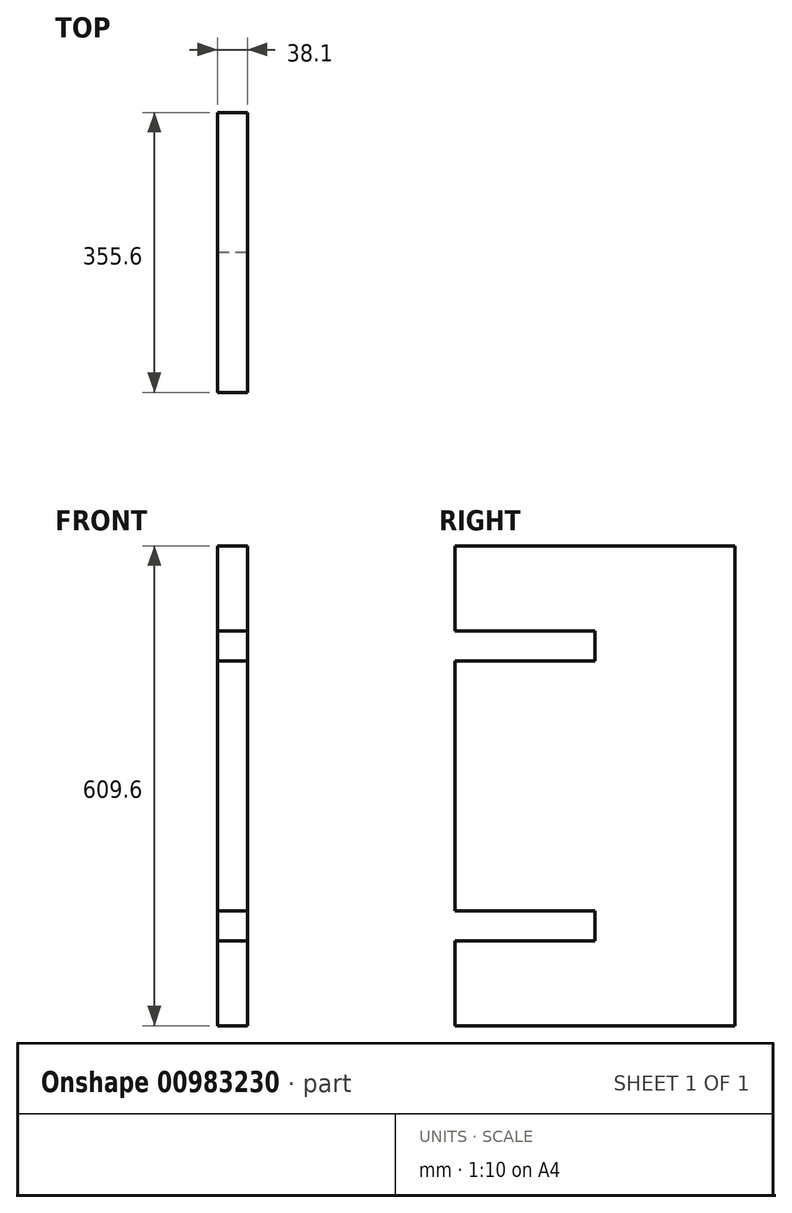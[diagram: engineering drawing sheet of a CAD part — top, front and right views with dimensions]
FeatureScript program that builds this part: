
annotation { "Feature Type Name" : "Feature", "Feature Type Description" : "" }
export const myFeature = defineFeature(function(context is Context, id is Id, definition is map)
    precondition{}
    {
        {
            var Q0;
            Q0=qCreatedBy(makeId("Right.planeOp"),FACE);
            var sketch = newSketch(context, id + "F0", { "sketchPlane" : qUnion([Q0])});
            skLineSegment(sketch, "E0.bottom", {"start": v(177.8, -304.8) * mm, "end": v(-177.8, -304.8) * mm});
            skLineSegment(sketch, "E0.top", {"start": v(177.8, 304.8) * mm, "end": v(-177.8, 304.8) * mm});
            skLineSegment(sketch, "E0.left", {"start": v(177.8, -304.8) * mm, "end": v(177.8, 304.8) * mm});
            skLineSegment(sketch, "E0.right", {"start": v(-177.8, -304.8) * mm, "end": v(-177.8, 304.8) * mm});
            skPoint(sketch, "E0.middle", {"position": v(0, 0) * mm});
            skLineSegment(sketch, "E1.bottom", {"start": v(-177.8, 196.85) * mm, "end": v(0, 196.85) * mm});
            skLineSegment(sketch, "E1.top", {"start": v(-177.8, 158.75) * mm, "end": v(0, 158.75) * mm});
            skLineSegment(sketch, "E1.left", {"start": v(-177.8, 196.85) * mm, "end": v(-177.8, 158.75) * mm});
            skLineSegment(sketch, "E1.right", {"start": v(0, 196.85) * mm, "end": v(0, 158.75) * mm});
            skLineSegment(sketch, "E2.MirrorCS", {"start": v(0, -196.85) * mm, "end": v(0, -158.75) * mm});
            skLineSegment(sketch, "E3.MirrorCS", {"start": v(-177.8, -196.85) * mm, "end": v(-177.8, -158.75) * mm});
            skLineSegment(sketch, "E4.MirrorCS", {"start": v(-177.8, -196.85) * mm, "end": v(0, -196.85) * mm});
            skLineSegment(sketch, "E5.MirrorCS", {"start": v(-177.8, -158.75) * mm, "end": v(0, -158.75) * mm});
            skSolve(sketch);
        }
        {
            var Q0;
            {var subQ7=sQuery(id+"F0.wireOp",EDGE,"E0.bottom");Q0=makeQuery(id+"F0.imprint","IMPRINT",FACE,{"disambiguationData":[TD([[makeQuery(id+"F0.imprint","IMPRINT",EDGE,{"derivedFrom":subQ7}),-1.0]])]});}
            extrude(context, id + "F1", {"entities" : qUnion([Q0]), "depth" : 38.1 * mm, "offsetDistance" : 25.4 * mm});
        }
    });
